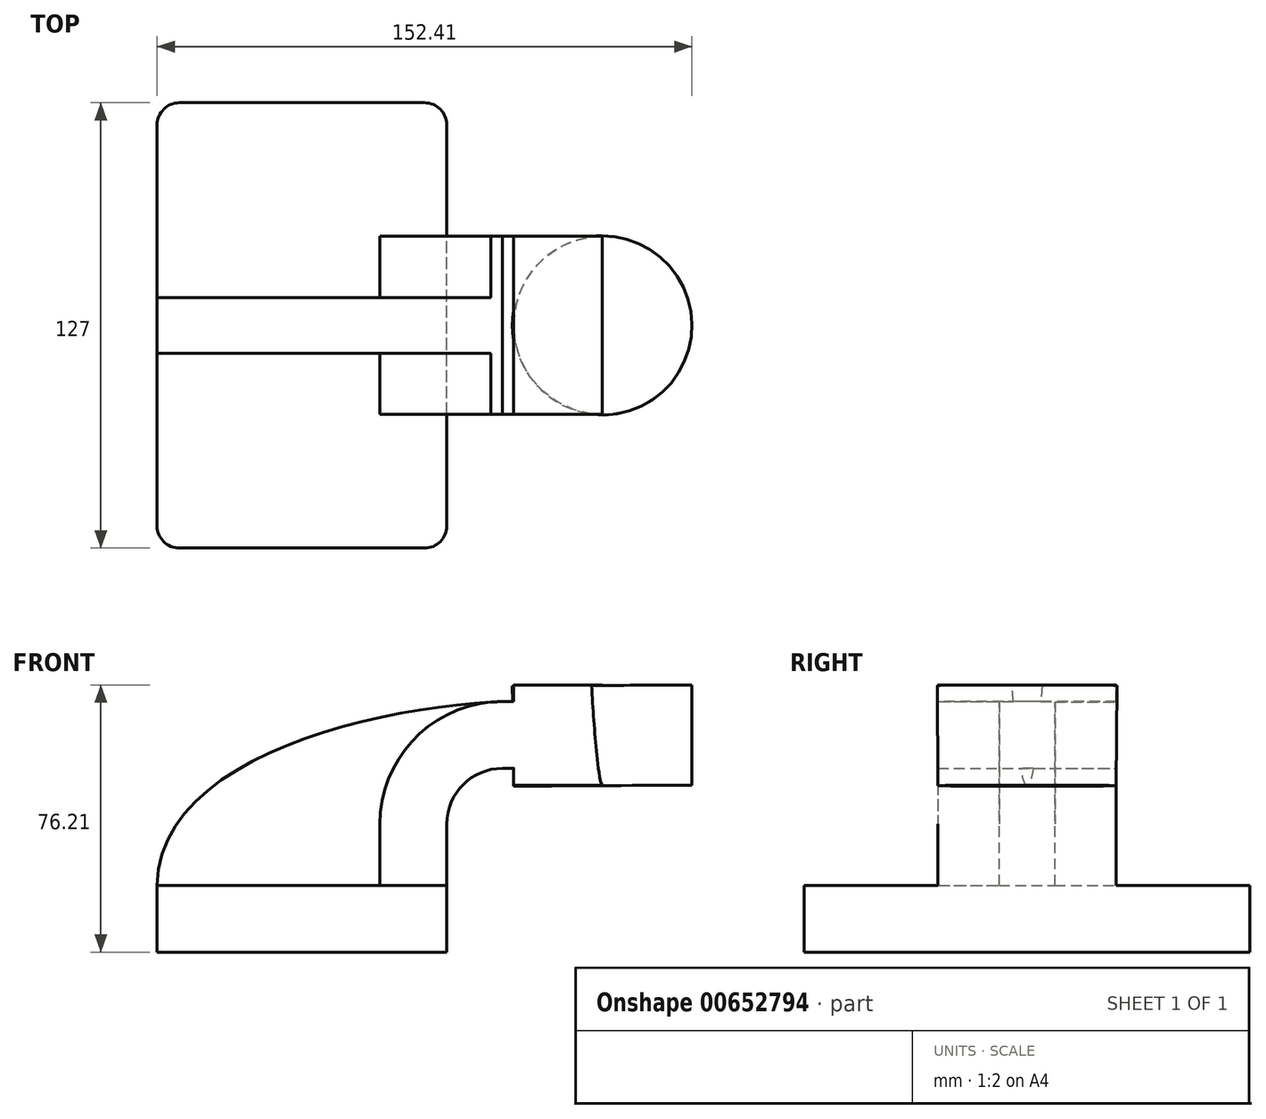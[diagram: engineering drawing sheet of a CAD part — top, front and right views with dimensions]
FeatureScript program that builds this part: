
annotation { "Feature Type Name" : "Feature", "Feature Type Description" : "" }
export const myFeature = defineFeature(function(context is Context, id is Id, definition is map)
    precondition{}
    {
        {
            var Q0;
            Q0=qCreatedBy(makeId("Front.planeOp"),FACE);
            var sketch = newSketch(context, id + "F0", { "sketchPlane" : qUnion([Q0])});
            skLineSegment(sketch, "E0.bottom", {"start": v(41.28, -9.52) * mm, "end": v(-41.28, -9.53) * mm});
            skLineSegment(sketch, "E0.top", {"start": v(41.28, 9.53) * mm, "end": v(-41.28, 9.53) * mm});
            skLineSegment(sketch, "E0.left", {"start": v(41.28, -9.52) * mm, "end": v(41.28, 9.53) * mm});
            skLineSegment(sketch, "E0.right", {"start": v(-41.28, -9.52) * mm, "end": v(-41.28, 9.53) * mm});
            skPoint(sketch, "E0.middle", {"position": v(0, 0) * mm});
            skLineSegment(sketch, "E1.bottom", {"start": v(60.32, 38.1) * mm, "end": v(111.13, 38.1) * mm});
            skLineSegment(sketch, "E1.top", {"start": v(60.32, 66.68) * mm, "end": v(111.12, 66.68) * mm});
            skLineSegment(sketch, "E1.left", {"start": v(60.32, 38.1) * mm, "end": v(60.32, 66.68) * mm});
            skLineSegment(sketch, "E1.right", {"start": v(111.13, 38.1) * mm, "end": v(111.12, 66.68) * mm});
            skPoint(sketch, "E1.middle", {"position": v(85.72, 52.39) * mm});
            skLineSegment(sketch, "E2", {"start": v(41.28, 9.53) * mm, "end": v(41.28, 27) * mm});
            skArc(sketch, "E3", {"start": v(41.27, 27) * mm, "mid": v(45.92, 38.23) * mm, "end": v(57.15, 42.88) * mm});
            skLineSegment(sketch, "E4", {"start": v(57.15, 42.88) * mm, "end": v(85.54, 42.88) * mm});
            skLineSegment(sketch, "E5.0", {"start": v(57.15, 61.93) * mm, "end": v(85.54, 61.93) * mm});
            skArc(sketch, "E5.1", {"start": v(22.23, 27) * mm, "mid": v(32.45, 51.7) * mm, "end": v(57.15, 61.93) * mm});
            skLineSegment(sketch, "E5.2", {"start": v(22.22, 9.53) * mm, "end": v(22.22, 27) * mm});
            skLineSegment(sketch, "E6", {"start": v(85.72, 38.1) * mm, "end": v(85.54, 66.68) * mm});
            skFitSpline(sketch, "E7", {"points": [v(-41.28, 9.52) * mm, v(57.15, 61.93) * mm], "startDerivative": vector(1.3, 110.96) * mm, "endDerivative": vector(105, 3.94) * mm});
            skSolve(sketch);
        }
        {
            var Q0;
            Q0=makeQuery(id+"F0.imprint","IMPRINT",FACE,{"disambiguationData":[TD([[makeQuery(id+"F0.imprint","IMPRINT",EDGE,{"derivedFrom":sQuery(id+"F0.wireOp",EDGE,"E0.bottom")}),-1.0]])]});
            extrude(context, id + "F1", {"entities" : qUnion([Q0]), "endBound" : BoundingType.SYMMETRIC, "depth" : 127 * mm, "offsetDistance" : 25.4 * mm});
        }
        {
            var Q0;
            {var subQ1=sQuery(id+"F0.wireOp",EDGE,"E2");Q0=makeQuery(id+"F0.imprint","IMPRINT",FACE,{"disambiguationData":[TD([[makeQuery(id+"F0.imprint","IMPRINT",EDGE,{"derivedFrom":subQ1}),1.0]])]});}
            var Q1;
            {var subQ4=sQuery(id+"F0.wireOp",EDGE,"E6");Q1=makeQuery(id+"F0.imprint","IMPRINT",FACE,{"disambiguationData":[TD([[makeQuery(id+"F0.imprint","IMPRINT",EDGE,{"derivedFrom":subQ4}),1.0]])]});}
            extrude(context, id + "F2", {"entities" : qUnion([Q0, Q1]), "operationType" : NewBodyOperationType.ADD, "endBound" : BoundingType.SYMMETRIC, "depth" : 50.8 * mm, "offsetDistance" : 25.4 * mm});
        }
        {
            var Q0;
            {var subQ3=sQuery(id+"F0.wireOp",EDGE,"E5.2");Q0=makeQuery(id+"F0.imprint","IMPRINT",FACE,{"disambiguationData":[TD([[makeQuery(id+"F0.imprint","IMPRINT",EDGE,{"derivedFrom":subQ3}),1.0]])]});}
            extrude(context, id + "F3", {"entities" : qUnion([Q0]), "operationType" : NewBodyOperationType.ADD, "endBound" : BoundingType.SYMMETRIC, "depth" : 15.88 * mm, "offsetDistance" : 25.4 * mm});
        }
        {
            var Q0;
            {var subQ0=sQuery(id+"F0.wireOp",EDGE,"E1.right");Q0=makeQuery(id+"F0.imprint","IMPRINT",FACE,{"disambiguationData":[TD([[makeQuery(id+"F0.imprint","IMPRINT",EDGE,{"derivedFrom":subQ0}),1.0]])]});}
            var Q1;
            Q1=sQuery(id+"F0.wireOp",EDGE,"E6");
            revolve(context, id + "F4", {"operationType" : NewBodyOperationType.ADD, "entities" : qUnion([Q0]), "axis" : qUnion([Q1]), "revolveType" : RevolveType.FULL});
        }
        {
            var Q0;
            Q0=makeQuery(id+"F1.opExtrude","CAP_EDGE",EDGE,{"disambiguationData":[OSD([sQuery(id+"F0.wireOp",EDGE,"E0.left")])],"isStart":false});
            var Q1;
            Q1=makeQuery(id+"F1.opExtrude","CAP_EDGE",EDGE,{"disambiguationData":[OSD([sQuery(id+"F0.wireOp",EDGE,"E0.right")])],"isStart":false});
            var Q2;
            Q2=makeQuery(id+"F1.opExtrude","CAP_EDGE",EDGE,{"disambiguationData":[OSD([sQuery(id+"F0.wireOp",EDGE,"E0.right")])],"isStart":true});
            var Q3;
            Q3=makeQuery(id+"F1.opExtrude","CAP_EDGE",EDGE,{"disambiguationData":[OSD([sQuery(id+"F0.wireOp",EDGE,"E0.left")])],"isStart":true});
            fillet(context, id + "F5", {"entities" : qUnion([Q0, Q1, Q2, Q3]), "radius" : 6.35 * mm, "tangentPropagation" : true, "allowEdgeOverflow" : false});
        }
    });
